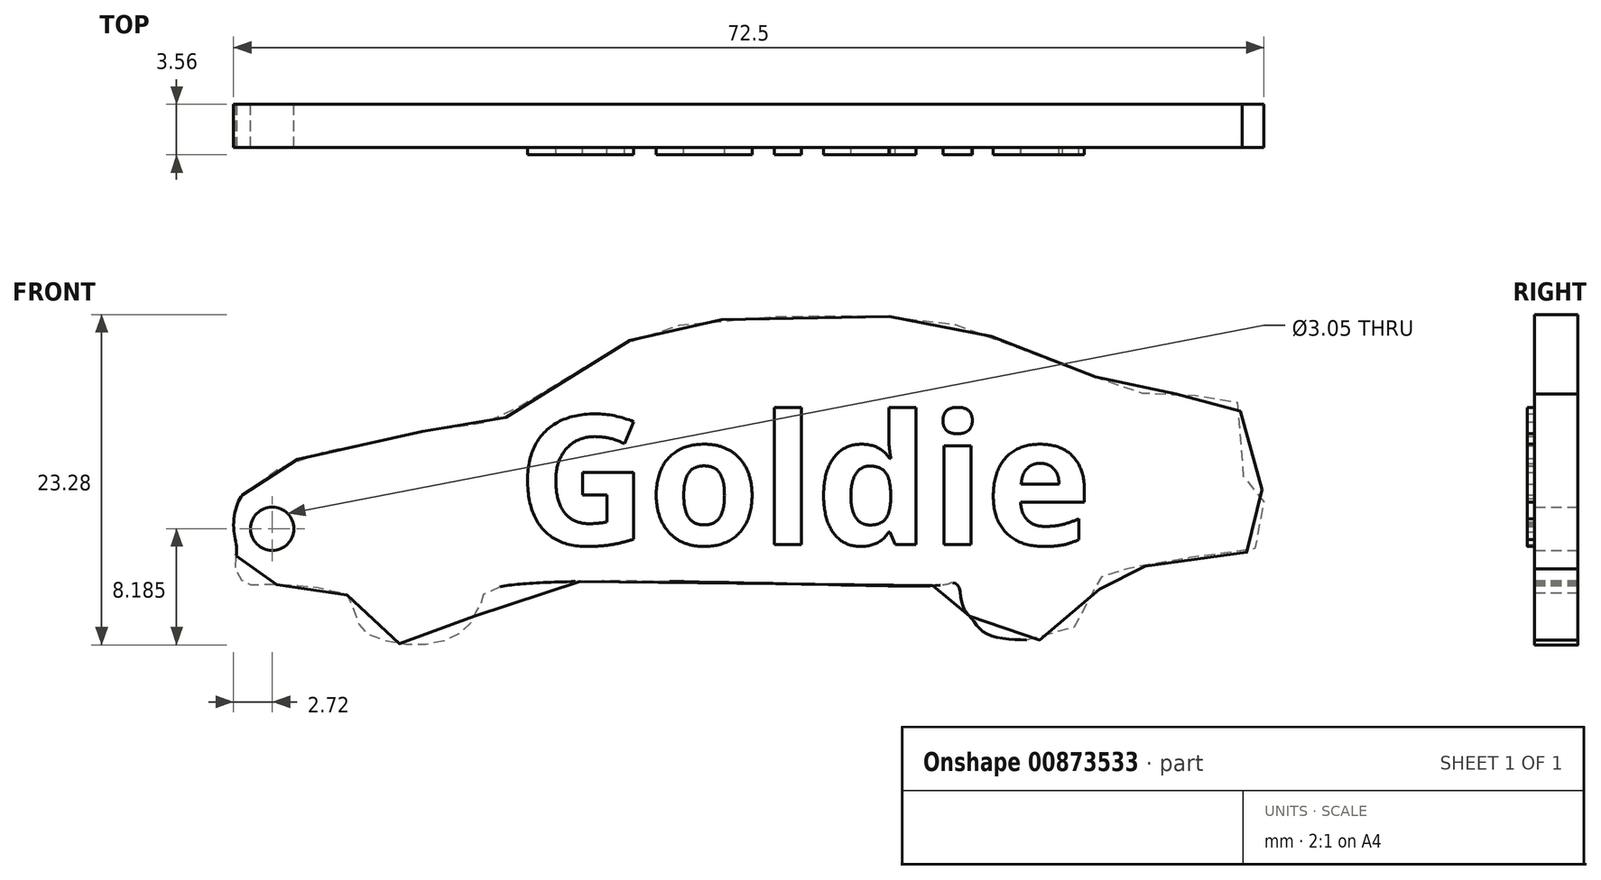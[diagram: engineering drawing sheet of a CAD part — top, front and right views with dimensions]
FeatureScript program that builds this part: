
annotation { "Feature Type Name" : "Feature", "Feature Type Description" : "" }
export const myFeature = defineFeature(function(context is Context, id is Id, definition is map)
    precondition{}
    {
        {
            var Q0;
            Q0=qCreatedBy(makeId("Front.planeOp"),FACE);
            var sketch = newSketch(context, id + "F0", { "sketchPlane" : qUnion([Q0])});
            skPoint(sketch, "E0.0.internal.snap0", {"position": v(-20.55, -6.22) * mm});
            skFitSpline(sketch, "E1", {"points": [v(-31.17, 1.06) * mm, v(-24.93, 2.54) * mm, v(-20.09, 3.2) * mm, v(-17.96, 3.6) * mm, v(-17.05, 3.85) * mm, v(-15.9, 4.75) * mm, v(-6.79, 9.93) * mm, v(-5.15, 10.25) * mm, v(-4.49, 10.42) * mm, v(5.12, 11.08) * mm, v(11.2, 10.83) * mm, v(15.13, 10.25) * mm, v(17.93, 9.19) * mm, v(22.6, 7.3) * mm, v(25.23, 6.4) * mm, v(27.61, 5.57) * mm, v(29.75, 5.5) * mm, v(31.97, 5.33) * mm, v(33.44, 5.16) * mm, v(34.43, 4.84) * mm, v(34.76, 0) * mm, v(35.09, -0.58) * mm, v(36.07, -1.16) * mm, v(36.24, -2.3) * mm, v(35.99, -4.6) * mm, v(35.5, -5.5) * mm, v(32.05, -5.92) * mm, v(28.76, -6.5) * mm, v(26.38, -6.82) * mm, v(25.56, -6.82) * mm, v(24.99, -6.9) * mm, v(24.66, -8.47) * mm, v(23.02, -10.85) * mm, v(21.3, -11.75) * mm, v(19.32, -11.83) * mm, v(16.78, -11.42) * mm, v(15.7, -10.35) * mm, v(15.05, -9.37) * mm, v(14.72, -7.97) * mm, v(14.31, -7.8) * mm, v(13.66, -7.97) * mm, v(-18.28, -8.3) * mm, v(-18.72, -9.03) * mm, v(-19.02, -9.53) * mm, v(-19.6, -10.68) * mm, v(-21.24, -11.83) * mm, v(-24.11, -12.16) * mm, v(-26.9, -11.34) * mm, v(-27.64, -10.1) * mm, v(-28.3, -8.63) * mm, v(-28.8, -8.55) * mm, v(-29.7, -8.3) * mm, v(-32.57, -7.97) * mm, v(-34.62, -7.97) * mm, v(-35.36, -7.9) * mm, v(-36.1, -6.82) * mm, v(-36.02, -5.5) * mm, v(-36.24, -4) * mm, v(-35.85, -2) * mm, v(-34.95, -1) * mm, v(-33.47, 0) * mm, v(-32.16, 0.73) * mm, v(-31.17, 1.06) * mm]});
            skArc(sketch, "E2", {"start": v(-35.61, -1.62) * mm, "mid": v(-36.68, -3.68) * mm, "end": v(-36.06, -5.91) * mm});
            skCircle(sketch, "E3.0", {"center": v(-33.52, -4) * mm, "radius": 1.52 * mm});
            skSolve(sketch);
        }
        {
            var Q0;
            Q0=makeQuery(id+"F0.imprint","IMPRINT",FACE,{"disambiguationData":[TD([[makeQuery(id+"F0.imprint","IMPRINT",EDGE,{"derivedFrom":sQuery(id+"F0.wireOp",EDGE,"E1")}),-1.0]])]});
            extrude(context, id + "F1", {"entities" : qUnion([Q0]), "depth" : 3.05 * mm, "offsetDistance" : 25.4 * mm});
        }
        {
            var Q0;
            Q0=makeQuery(id+"F1.opExtrude","CAP_FACE",FACE,{"disambiguationData":[OSD([sQuery(id+"F0.wireOp",EDGE,"E1"),sQuery(id+"F0.wireOp",EDGE,"E2"),sQuery(id+"F0.wireOp",EDGE,"E3.0")])],"isStart":false});
            var sketch = newSketch(context, id + "F2", { "sketchPlane" : qUnion([Q0])});
            skText(sketch, "E4", { "text": "Goldie", "fontName": "OpenSans-Bold.ttf"});
            const initialGuessF2  = {"E4": [-0.01629, -0.00513, 1, 0, 0.00917]};
            skSetInitialGuess(sketch, initialGuessF2);
            skSolve(sketch);
        }
        {
            var Q0;
            Q0 = qSketchRegion(id + "F2", true);
            extrude(context, id + "F3", {"entities" : qUnion([Q0]), "operationType" : NewBodyOperationType.ADD, "depth" : 0.5 * mm, "offsetDistance" : 25.4 * mm});
        }
    });
